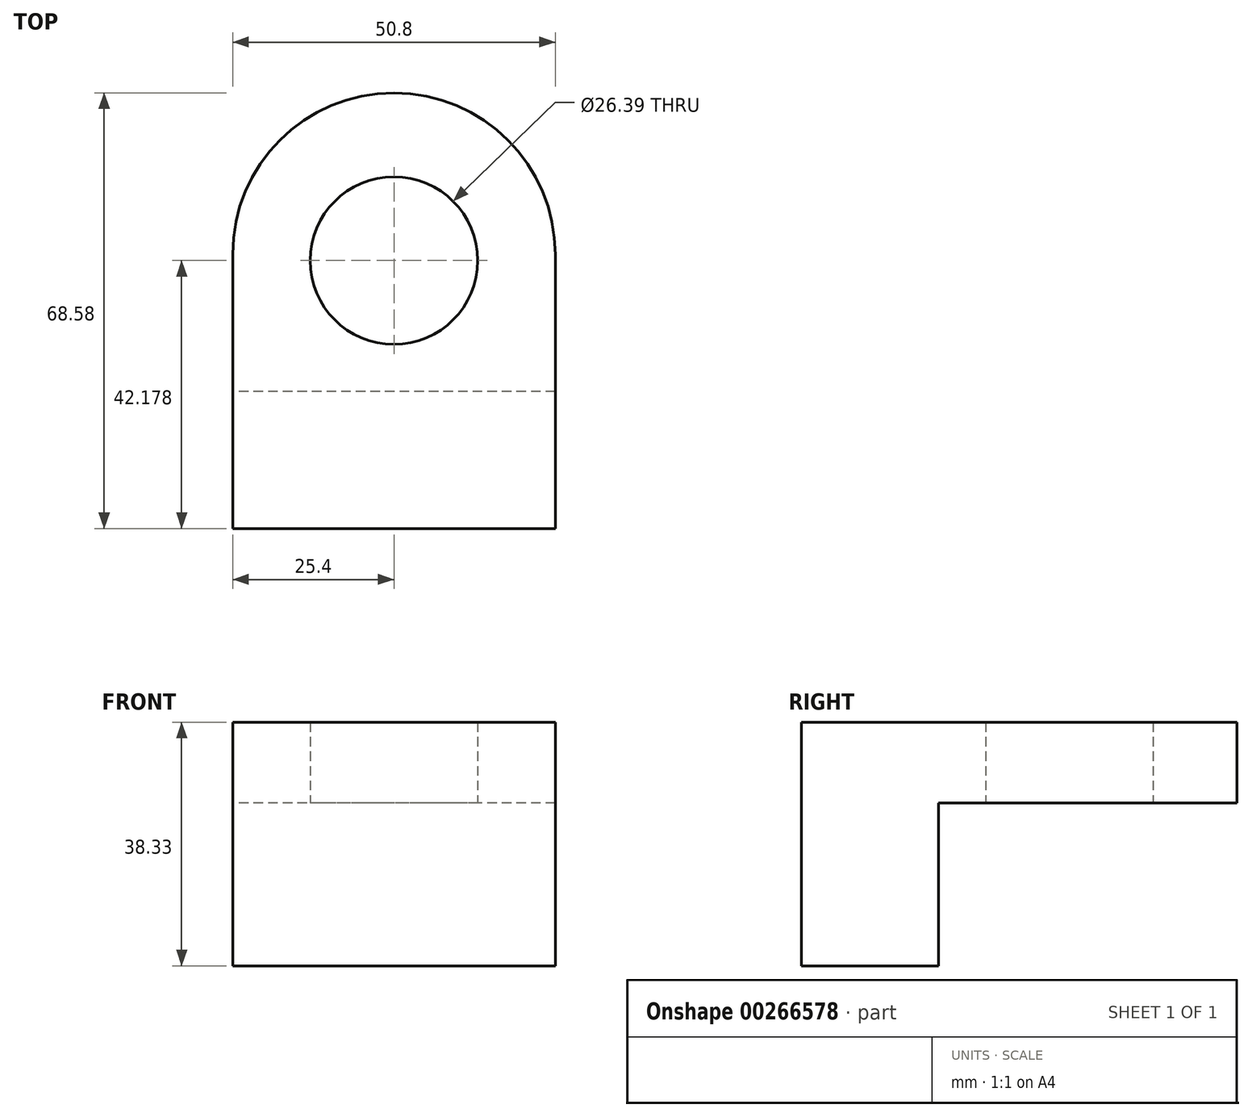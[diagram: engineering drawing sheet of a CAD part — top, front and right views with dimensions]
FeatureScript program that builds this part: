
annotation { "Feature Type Name" : "Feature", "Feature Type Description" : "" }
export const myFeature = defineFeature(function(context is Context, id is Id, definition is map)
    precondition{}
    {
        {
            var Q0;
            Q0=qCreatedBy(makeId("Top.planeOp"),FACE);
            var sketch = newSketch(context, id + "F0", { "sketchPlane" : qUnion([Q0])});
            skLineSegment(sketch, "E0.bottom", {"start": v(-25.4, 21.59) * mm, "end": v(25.4, 21.59) * mm});
            skLineSegment(sketch, "E0.top", {"start": v(-25.4, -21.59) * mm, "end": v(25.4, -21.59) * mm});
            skLineSegment(sketch, "E0.left", {"start": v(-25.4, 21.59) * mm, "end": v(-25.4, -21.59) * mm});
            skLineSegment(sketch, "E0.right", {"start": v(25.4, 21.6) * mm, "end": v(25.4, -21.59) * mm});
            skPoint(sketch, "E0.middle", {"position": v(0, 0) * mm});
            skArc(sketch, "E1", {"start": v(25.4, 21.59) * mm, "mid": v(0, 47) * mm, "end": v(-25.4, 21.6) * mm});
            skSolve(sketch);
        }
        {
            var Q0;
            Q0 = qSketchRegion(id + "F0", true);
            extrude(context, id + "F1", {"entities" : qUnion([Q0]), "depth" : 12.7 * mm});
        }
        {
            var Q0;
            Q0=qCreatedBy(makeId("Top.planeOp"),FACE);
            var sketch = newSketch(context, id + "F2", { "sketchPlane" : qUnion([Q0])});
            skCircle(sketch, "E2", {"center": v(0, 20.59) * mm, "radius": 13.2 * mm});
            skSolve(sketch);
        }
        {
            var Q0;
            Q0=makeQuery(id+"F2.imprint","IMPRINT",FACE,{"disambiguationData":[TD([[makeQuery(id+"F2.imprint","IMPRINT",EDGE,{"derivedFrom":sQuery(id+"F2.wireOp",EDGE,"E2")}),1.0]])]});
            extrude(context, id + "F3", {"entities" : qUnion([Q0]), "operationType" : NewBodyOperationType.REMOVE, "endBound" : BoundingType.THROUGH_ALL, "depth" : 25.4 * mm});
        }
        {
            var Q0;
            Q0=qCreatedBy(makeId("Front.planeOp"),FACE);
            var sketch = newSketch(context, id + "F4", { "sketchPlane" : qUnion([Q0])});
            skLineSegment(sketch, "E3.bottom", {"start": v(25.4, 0) * mm, "end": v(-25.4, 0) * mm});
            skLineSegment(sketch, "E3.top", {"start": v(25.4, -25.63) * mm, "end": v(-25.4, -25.63) * mm});
            skLineSegment(sketch, "E3.left", {"start": v(25.4, 0) * mm, "end": v(25.4, -25.63) * mm});
            skLineSegment(sketch, "E3.right", {"start": v(-25.4, 0) * mm, "end": v(-25.4, -25.63) * mm});
            skSolve(sketch);
        }
        {
            var Q0;
            Q0=makeQuery(id+"F4.imprint","IMPRINT",FACE,{"disambiguationData":[TD([[makeQuery(id+"F4.imprint","IMPRINT",EDGE,{"derivedFrom":sQuery(id+"F4.wireOp",EDGE,"E3.bottom")}),1.0]])]});
            extrude(context, id + "F5", {"entities" : qUnion([Q0]), "operationType" : NewBodyOperationType.ADD, "depth" : 21.59 * mm});
        }
    });
